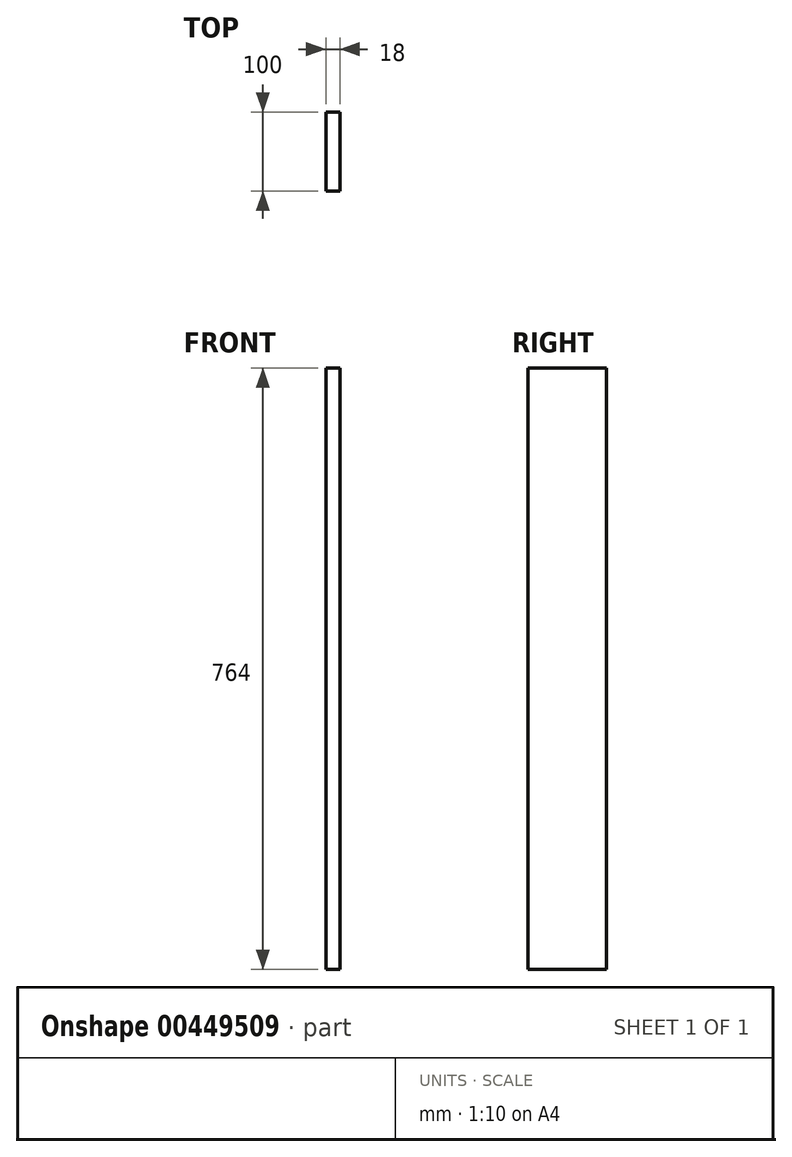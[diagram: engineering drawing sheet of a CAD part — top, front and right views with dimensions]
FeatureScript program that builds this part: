
annotation { "Feature Type Name" : "Feature", "Feature Type Description" : "" }
export const myFeature = defineFeature(function(context is Context, id is Id, definition is map)
    precondition{}
    {
        {
            var Q0;
            Q0=qCreatedBy(makeId("Right.planeOp"),FACE);
            var sketch = newSketch(context, id + "F0", { "sketchPlane" : qUnion([Q0])});
            skLineSegment(sketch, "E0.bottom", {"start": v(0, 764) * mm, "end": v(100, 764) * mm});
            skLineSegment(sketch, "E0.top", {"start": v(0, 0) * mm, "end": v(100, 0) * mm});
            skLineSegment(sketch, "E0.left", {"start": v(0, 764) * mm, "end": v(0, 0) * mm});
            skLineSegment(sketch, "E0.right", {"start": v(100, 764) * mm, "end": v(100, 0) * mm});
            skSolve(sketch);
        }
        {
            var Q0;
            Q0 = qSketchRegion(id + "F0", true);
            extrude(context, id + "F1", {"entities" : qUnion([Q0]), "depth" : 18 * mm});
        }
    });
